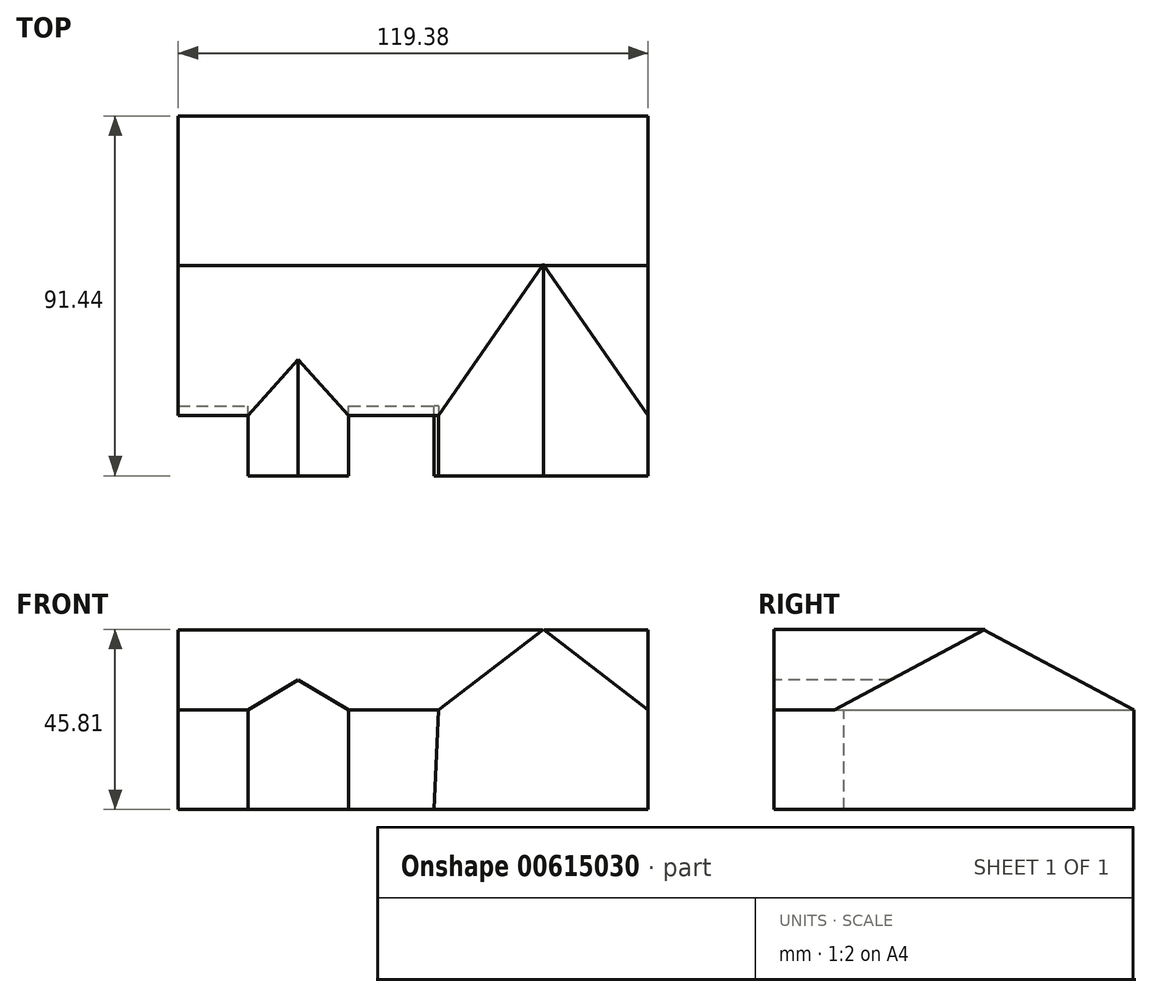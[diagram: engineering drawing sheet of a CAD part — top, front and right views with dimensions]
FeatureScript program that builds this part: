
annotation { "Feature Type Name" : "Feature", "Feature Type Description" : "" }
export const myFeature = defineFeature(function(context is Context, id is Id, definition is map)
    precondition{}
    {
        {
            var Q0;
            Q0=qCreatedBy(makeId("Front.planeOp"),FACE);
            var sketch = newSketch(context, id + "F0", { "sketchPlane" : qUnion([Q0])});
            skLineSegment(sketch, "E0.bottom", {"start": v(-64.93, 0) * mm, "end": v(54.43, 0) * mm});
            skLineSegment(sketch, "E0.top", {"start": v(-64.93, 25.39) * mm, "end": v(54.43, 25.39) * mm});
            skLineSegment(sketch, "E0.left", {"start": v(-64.93, 0) * mm, "end": v(-64.93, 25.39) * mm});
            skLineSegment(sketch, "E0.right", {"start": v(54.43, 0) * mm, "end": v(54.43, 25.39) * mm});
            skSolve(sketch);
        }
        {
            var Q0;
            Q0 = qSketchRegion(id + "F0", true);
            extrude(context, id + "F1", {"entities" : qUnion([Q0]), "depth" : 73.66 * mm, "offsetDistance" : 25.4 * mm});
        }
        {
            var Q0;
            Q0=makeQuery(id+"F1.opExtrude","SWEPT_FACE",FACE,{"disambiguationData":[OSD([sQuery(id+"F0.wireOp",EDGE,"E0.right")])]});
            var sketch = newSketch(context, id + "F2", { "sketchPlane" : qUnion([Q0])});
            skLineSegment(sketch, "E1", {"start": v(0, 25.39) * mm, "end": v(-38.07, 25.39) * mm});
            skLineSegment(sketch, "E2", {"start": v(-38.07, 25.39) * mm, "end": v(-38.07, 45.68) * mm});
            skLineSegment(sketch, "E3", {"start": v(-38.07, 45.68) * mm, "end": v(0, 25.39) * mm});
            skLineSegment(sketch, "E4", {"start": v(-38.07, 25.39) * mm, "end": v(-76.13, 25.39) * mm});
            skLineSegment(sketch, "E5", {"start": v(-76.13, 25.39) * mm, "end": v(-38.07, 45.68) * mm});
            skSolve(sketch);
        }
        {
            var Q0;
            Q0 = qSketchRegion(id + "F2", true);
            extrude(context, id + "F3", {"entities" : qUnion([Q0]), "operationType" : NewBodyOperationType.ADD, "oppositeDirection" : true, "depth" : 119.38 * mm, "offsetDistance" : 25.4 * mm});
        }
        {
            var Q0;
            Q0=makeQuery(id+"F1.opExtrude","CAP_FACE",FACE,{"disambiguationData":[OSD([sQuery(id+"F0.wireOp",EDGE,"E0.bottom"),sQuery(id+"F0.wireOp",EDGE,"E0.top"),sQuery(id+"F0.wireOp",EDGE,"E0.left"),sQuery(id+"F0.wireOp",EDGE,"E0.right")])],"isStart":false});
            var sketch = newSketch(context, id + "F4", { "sketchPlane" : qUnion([Q0])});
            skLineSegment(sketch, "E6", {"start": v(54.43, 25.39) * mm, "end": v(27.83, 25.39) * mm});
            skLineSegment(sketch, "E7", {"start": v(27.83, 25.39) * mm, "end": v(27.83, 45.81) * mm});
            skLineSegment(sketch, "E8", {"start": v(27.83, 45.81) * mm, "end": v(54.43, 25.39) * mm});
            skLineSegment(sketch, "E9", {"start": v(27.83, 25.39) * mm, "end": v(1.16, 25.39) * mm});
            skLineSegment(sketch, "E10", {"start": v(1.16, 25.39) * mm, "end": v(27.83, 45.81) * mm});
            skLineSegment(sketch, "E11", {"start": v(-64.93, 25.39) * mm, "end": v(-47.16, 25.39) * mm});
            skLineSegment(sketch, "E12", {"start": v(-47.16, 25.39) * mm, "end": v(-34.44, 25.39) * mm});
            skLineSegment(sketch, "E13", {"start": v(-34.44, 25.39) * mm, "end": v(-34.44, 33) * mm});
            skLineSegment(sketch, "E14", {"start": v(-34.44, 33) * mm, "end": v(-47.16, 25.39) * mm});
            skLineSegment(sketch, "E15", {"start": v(-34.44, 25.39) * mm, "end": v(-21.65, 25.39) * mm});
            skLineSegment(sketch, "E16", {"start": v(-21.65, 25.39) * mm, "end": v(-34.44, 33) * mm});
            skLineSegment(sketch, "E17", {"start": v(-47.16, 25.39) * mm, "end": v(-47.16, 0) * mm});
            skLineSegment(sketch, "E18", {"start": v(-47.16, 0) * mm, "end": v(-21.65, 0) * mm});
            skLineSegment(sketch, "E19", {"start": v(-21.65, 0) * mm, "end": v(-21.65, 25.39) * mm});
            skLineSegment(sketch, "E20", {"start": v(1.16, 25.39) * mm, "end": v(0, 0) * mm});
            skLineSegment(sketch, "E21", {"start": v(0, 0) * mm, "end": v(54.43, 0) * mm});
            skLineSegment(sketch, "E22", {"start": v(54.43, 0) * mm, "end": v(54.43, 25.39) * mm});
            skSolve(sketch);
        }
        {
            var Q0;
            Q0=makeQuery(id+"F4.imprint","IMPRINT",FACE,{"disambiguationData":[TD([[makeQuery(id+"F4.imprint","IMPRINT",EDGE,{"derivedFrom":sQuery(id+"F4.wireOp",EDGE,"E13")}),-1.0]])]});
            var Q1;
            Q1=makeQuery(id+"F4.imprint","IMPRINT",FACE,{"disambiguationData":[TD([[makeQuery(id+"F4.imprint","IMPRINT",EDGE,{"derivedFrom":sQuery(id+"F4.wireOp",EDGE,"E6")}),1.0]])]});
            var Q2;
            Q2=makeQuery(id+"F4.imprint","IMPRINT",FACE,{"disambiguationData":[TD([[makeQuery(id+"F4.imprint","IMPRINT",EDGE,{"derivedFrom":sQuery(id+"F4.wireOp",EDGE,"E7")}),1.0]])]});
            var Q3;
            Q3=makeQuery(id+"F4.imprint","IMPRINT",FACE,{"disambiguationData":[TD([[makeQuery(id+"F4.imprint","IMPRINT",EDGE,{"derivedFrom":sQuery(id+"F4.wireOp",EDGE,"E12")}),1.0]])]});
            extrude(context, id + "F5", {"entities" : qUnion([Q0, Q1, Q2, Q3]), "operationType" : NewBodyOperationType.ADD, "oppositeDirection" : true, "depth" : 35.81 * mm, "offsetDistance" : 25.4 * mm});
        }
        {
            var Q0;
            Q0 = qSketchRegion(id + "F4", true);
            extrude(context, id + "F6", {"entities" : qUnion([Q0]), "operationType" : NewBodyOperationType.ADD, "depth" : 17.78 * mm, "offsetDistance" : 25.4 * mm});
        }
    });
